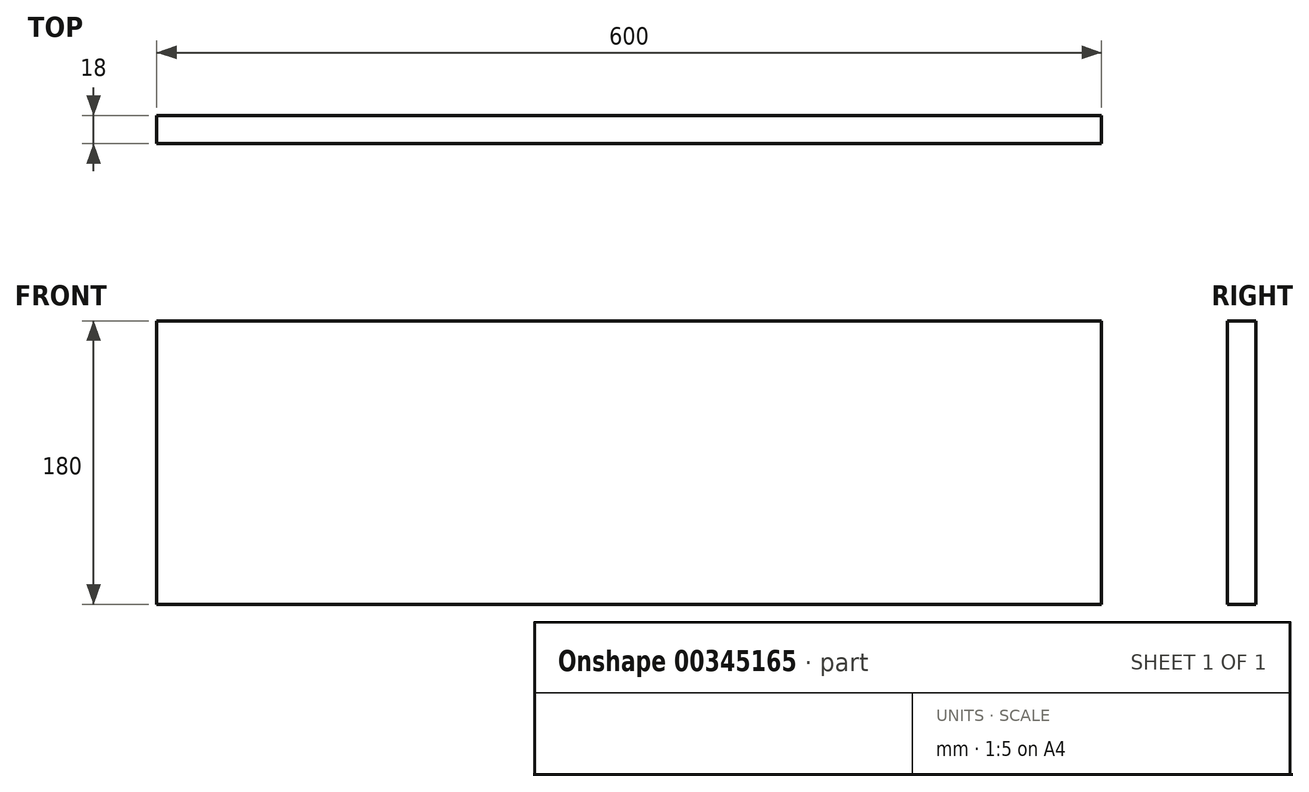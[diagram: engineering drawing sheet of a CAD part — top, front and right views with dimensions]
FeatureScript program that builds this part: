
annotation { "Feature Type Name" : "Feature", "Feature Type Description" : "" }
export const myFeature = defineFeature(function(context is Context, id is Id, definition is map)
    precondition{}
    {
        {
            var Q0;
            Q0=qCreatedBy(makeId("Front.planeOp"),FACE);
            var sketch = newSketch(context, id + "F0", { "sketchPlane" : qUnion([Q0])});
            skLineSegment(sketch, "E0.bottom", {"start": v(0, 0) * mm, "end": v(52.5, 0) * mm});
            skLineSegment(sketch, "E0.top", {"start": v(0, 35.38) * mm, "end": v(52.5, 35.38) * mm});
            skLineSegment(sketch, "E0.left", {"start": v(0, 0) * mm, "end": v(0, 35.38) * mm});
            skLineSegment(sketch, "E0.right", {"start": v(52.5, 0) * mm, "end": v(52.5, 35.38) * mm});
            skSolve(sketch);
        }
        {
            var Q0;
            Q0=makeQuery(id+"F0.imprint","IMPRINT",FACE,{"disambiguationData":[TD([[makeQuery(id+"F0.imprint","IMPRINT",EDGE,{"derivedFrom":sQuery(id+"F0.wireOp",EDGE,"E0.bottom")}),1.0]])]});
            extrude(context, id + "F1", {"entities" : qUnion([Q0]), "depth" : 18 * mm});
        }
        {
            var Q0;
            Q0=makeQuery(id+"F1.opExtrude","SWEPT_FACE",FACE,{"disambiguationData":[OSD([sQuery(id+"F0.wireOp",EDGE,"E0.left")])]});
            extrude(context, id + "F2", {"entities" : qUnion([Q0]), "operationType" : NewBodyOperationType.ADD, "oppositeDirection" : true, "depth" : 600 * mm});
        }
        {
            var Q0;
            {var subQ0=sQuery(id+"F0.wireOp",EDGE,"E0.bottom");Q0=makeQuery(id+"F2.boolean.opBoolean","MERGE",FACE,{"derivedFrom":[makeQuery(id+"F1.opExtrude","SWEPT_FACE",FACE,{"disambiguationData":[OSD([subQ0])]}),makeQuery(id+"F2.opExtrude","SWEPT_FACE",FACE,{"disambiguationData":[OSD([subQ0,sQuery(id+"F0.wireOp",EDGE,"E0.left")])]})]});}
            extrude(context, id + "F3", {"entities" : qUnion([Q0]), "operationType" : NewBodyOperationType.ADD, "oppositeDirection" : true, "depth" : 180 * mm});
        }
    });
